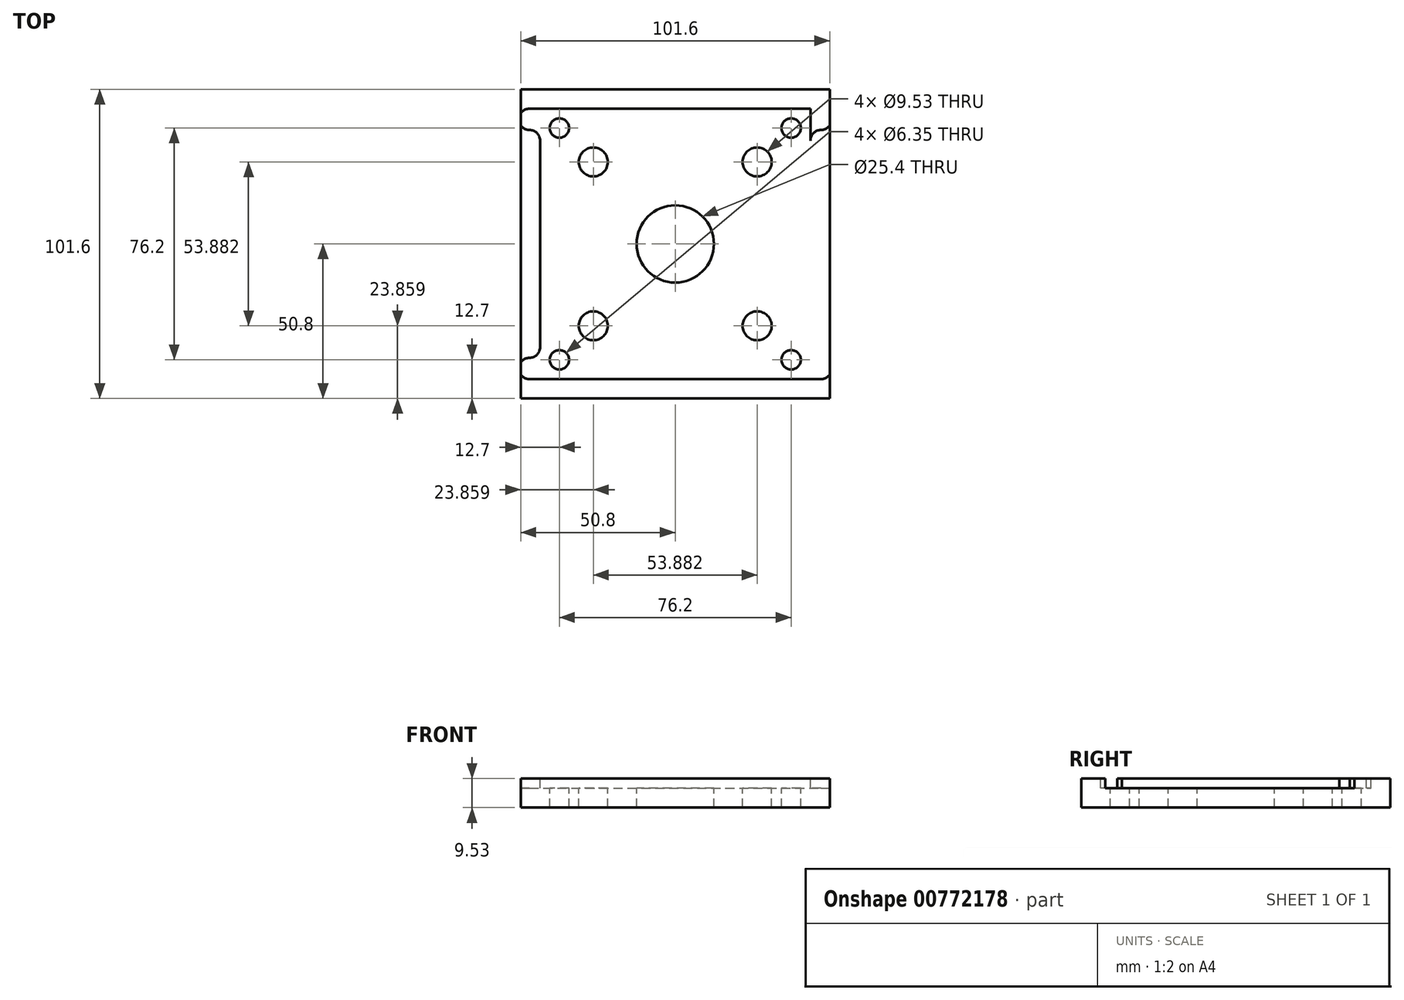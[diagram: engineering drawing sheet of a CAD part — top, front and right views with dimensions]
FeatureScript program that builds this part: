
annotation { "Feature Type Name" : "Feature", "Feature Type Description" : "" }
export const myFeature = defineFeature(function(context is Context, id is Id, definition is map)
    precondition{}
    {
        {
            var Q0;
            Q0=qCreatedBy(makeId("Top.planeOp"),FACE);
            var sketch = newSketch(context, id + "F0", { "sketchPlane" : qUnion([Q0])});
            skLineSegment(sketch, "E0.bottom", {"start": v(0, 0) * mm, "end": v(101.6, 0) * mm});
            skLineSegment(sketch, "E0.top", {"start": v(0, 101.6) * mm, "end": v(101.6, 101.6) * mm});
            skLineSegment(sketch, "E0.left", {"start": v(0, 0) * mm, "end": v(0, 101.6) * mm});
            skLineSegment(sketch, "E0.right", {"start": v(101.6, 0) * mm, "end": v(101.6, 101.6) * mm});
            skSolve(sketch);
        }
        {
            var Q0;
            Q0=makeQuery(id+"F0.imprint","IMPRINT",FACE,{"disambiguationData":[TD([[makeQuery(id+"F0.imprint","IMPRINT",EDGE,{"derivedFrom":sQuery(id+"F0.wireOp",EDGE,"E0.bottom")}),1.0]])]});
            extrude(context, id + "F1", {"entities" : qUnion([Q0]), "depth" : 9.52 * mm, "offsetDistance" : 25.4 * mm});
        }
        {
            var Q0;
            Q0=makeQuery(id+"F1.opExtrude","CAP_FACE",FACE,{"disambiguationData":[OSD([sQuery(id+"F0.wireOp",EDGE,"E0.bottom"),sQuery(id+"F0.wireOp",EDGE,"E0.top"),sQuery(id+"F0.wireOp",EDGE,"E0.left"),sQuery(id+"F0.wireOp",EDGE,"E0.right")])],"isStart":false});
            var sketch = newSketch(context, id + "F2", { "sketchPlane" : qUnion([Q0])});
            skLineSegment(sketch, "E1.bottom", {"start": v(6.35, 6.35) * mm, "end": v(95.25, 6.35) * mm});
            skLineSegment(sketch, "E1.top", {"start": v(6.35, 95.25) * mm, "end": v(95.25, 95.25) * mm});
            skLineSegment(sketch, "E1.left", {"start": v(6.35, 6.35) * mm, "end": v(6.35, 95.25) * mm});
            skLineSegment(sketch, "E1.right", {"start": v(95.25, 6.35) * mm, "end": v(95.25, 95.25) * mm});
            skSolve(sketch);
        }
        {
            var Q0;
            Q0=makeQuery(id+"F2.imprint","IMPRINT",FACE,{"disambiguationData":[TD([[makeQuery(id+"F2.imprint","IMPRINT",EDGE,{"derivedFrom":sQuery(id+"F2.wireOp",EDGE,"E1.bottom")}),1.0]])]});
            extrude(context, id + "F3", {"entities" : qUnion([Q0]), "operationType" : NewBodyOperationType.REMOVE, "oppositeDirection" : true, "depth" : 3.17 * mm, "offsetDistance" : 25.4 * mm});
        }
        {
            var Q0;
            Q0=makeQuery(id+"F1.opExtrude","CAP_FACE",FACE,{"disambiguationData":[OSD([sQuery(id+"F0.wireOp",EDGE,"E0.bottom"),sQuery(id+"F0.wireOp",EDGE,"E0.top"),sQuery(id+"F0.wireOp",EDGE,"E0.left"),sQuery(id+"F0.wireOp",EDGE,"E0.right")])],"isStart":false});
            var sketch = newSketch(context, id + "F4", { "sketchPlane" : qUnion([Q0])});
            skArc(sketch, "E2", {"start": v(2.86, 95.25) * mm, "mid": v(-0.64, 91.76) * mm, "end": v(2.86, 88.27) * mm});
            skLineSegment(sketch, "E3.0.0", {"start": v(95.25, 95.25) * mm, "end": v(6.35, 95.25) * mm});
            skLineSegment(sketch, "E3.0.1", {"start": v(6.35, 95.25) * mm, "end": v(6.35, 6.35) * mm});
            skLineSegment(sketch, "E3.0.2", {"start": v(6.35, 6.35) * mm, "end": v(95.25, 6.35) * mm});
            skLineSegment(sketch, "E3.0.3", {"start": v(95.25, 6.35) * mm, "end": v(95.25, 95.25) * mm});
            skLineSegment(sketch, "E4", {"start": v(6.35, 95.25) * mm, "end": v(2.86, 95.25) * mm});
            skArc(sketch, "E5", {"start": v(6.35, 84.77) * mm, "mid": v(5.33, 87.24) * mm, "end": v(2.86, 88.27) * mm});
            skLineSegment(sketch, "E6", {"start": v(6.35, 84.77) * mm, "end": v(6.35, 95.25) * mm});
            skLineSegment(sketch, "E7", {"start": v(50.8, 95.25) * mm, "end": v(50.8, 6.35) * mm, "construction": true});
            skLineSegment(sketch, "E8", {"start": v(6.35, 50.8) * mm, "end": v(95.25, 50.8) * mm, "construction": true});
            skArc(sketch, "E9.MirrorCS", {"start": v(98.74, 95.25) * mm, "mid": v(102.23, 91.76) * mm, "end": v(98.74, 88.27) * mm});
            skArc(sketch, "E10.MirrorCS", {"start": v(95.25, 84.77) * mm, "mid": v(96.27, 87.24) * mm, "end": v(98.74, 88.27) * mm});
            skLineSegment(sketch, "E11.MirrorCS", {"start": v(95.25, 95.25) * mm, "end": v(98.74, 95.25) * mm});
            skLineSegment(sketch, "E12.MirrorCS", {"start": v(6.35, 6.35) * mm, "end": v(2.86, 6.35) * mm});
            skArc(sketch, "E13.MirrorCS", {"start": v(2.86, 6.35) * mm, "mid": v(-0.64, 9.84) * mm, "end": v(2.86, 13.33) * mm});
            skArc(sketch, "E14.MirrorCS", {"start": v(6.35, 16.83) * mm, "mid": v(5.33, 14.36) * mm, "end": v(2.86, 13.33) * mm});
            skArc(sketch, "E15.MirrorCS", {"start": v(98.74, 6.35) * mm, "mid": v(102.23, 9.84) * mm, "end": v(98.74, 13.33) * mm});
            skLineSegment(sketch, "E16.MirrorCS", {"start": v(95.25, 6.35) * mm, "end": v(98.74, 6.35) * mm});
            skArc(sketch, "E17.MirrorCS", {"start": v(95.25, 16.83) * mm, "mid": v(96.27, 14.36) * mm, "end": v(98.74, 13.33) * mm});
            skSolve(sketch);
        }
        {
            var Q0;
            Q0=makeQuery(id+"F4.imprint","IMPRINT",FACE,{"disambiguationData":[TD([[makeQuery(id+"F4.imprint","IMPRINT",EDGE,{"derivedFrom":sQuery(id+"F4.wireOp",EDGE,"E2")}),1.0]])]});
            var Q1;
            {var subQ0=sQuery(id+"F4.wireOp",EDGE,"E12.MirrorCS");Q1=makeQuery(id+"F4.imprint","IMPRINT",FACE,{"disambiguationData":[TD([[makeQuery(id+"F4.imprint","IMPRINT",EDGE,{"derivedFrom":subQ0}),-1.0]])]});}
            var Q2;
            Q2=makeQuery(id+"F4.imprint","IMPRINT",FACE,{"disambiguationData":[TD([[makeQuery(id+"F4.imprint","IMPRINT",EDGE,{"derivedFrom":sQuery(id+"F4.wireOp",EDGE,"E15.MirrorCS")}),1.0]])]});
            var Q3;
            Q3=makeQuery(id+"F4.imprint","IMPRINT",FACE,{"disambiguationData":[TD([[makeQuery(id+"F4.imprint","IMPRINT",EDGE,{"derivedFrom":sQuery(id+"F4.wireOp",EDGE,"E9.MirrorCS")}),-1.0]])]});
            extrude(context, id + "F5", {"entities" : qUnion([Q0, Q1, Q2, Q3]), "operationType" : NewBodyOperationType.REMOVE, "oppositeDirection" : true, "depth" : 3.17 * mm, "offsetDistance" : 25.4 * mm});
        }
        {
            var Q0;
            {var subQ0=sQuery(id+"F4.wireOp",EDGE,"E3.0.3");Q0=makeQuery(id+"F5.boolean.opBoolean","MERGE",FACE,{"derivedFrom":[makeQuery(id+"F3.boolean.opBoolean","COPY",FACE,{"derivedFrom":makeQuery(id+"F3.opExtrude","CAP_FACE",FACE,{"disambiguationData":[OSD([sQuery(id+"F2.wireOp",EDGE,"E1.bottom"),sQuery(id+"F2.wireOp",EDGE,"E1.top"),sQuery(id+"F2.wireOp",EDGE,"E1.left"),sQuery(id+"F2.wireOp",EDGE,"E1.right")])],"isStart":false})}),makeQuery(id+"F5.opExtrude","CAP_FACE",FACE,{"disambiguationData":[OSD([sQuery(id+"F4.wireOp",EDGE,"E2"),sQuery(id+"F4.wireOp",EDGE,"E4"),sQuery(id+"F4.wireOp",EDGE,"E5"),sQuery(id+"F4.wireOp",EDGE,"E6")])],"isStart":false}),makeQuery(id+"F5.opExtrude","CAP_FACE",FACE,{"disambiguationData":[OSD([sQuery(id+"F4.wireOp",EDGE,"E3.0.1"),sQuery(id+"F4.wireOp",EDGE,"E12.MirrorCS"),sQuery(id+"F4.wireOp",EDGE,"E13.MirrorCS"),sQuery(id+"F4.wireOp",EDGE,"E14.MirrorCS")])],"isStart":false}),makeQuery(id+"F5.opExtrude","CAP_FACE",FACE,{"disambiguationData":[OSD([subQ0,sQuery(id+"F4.wireOp",EDGE,"E15.MirrorCS"),sQuery(id+"F4.wireOp",EDGE,"E16.MirrorCS"),sQuery(id+"F4.wireOp",EDGE,"E17.MirrorCS")])],"isStart":false}),makeQuery(id+"F5.opExtrude","CAP_FACE",FACE,{"disambiguationData":[OSD([subQ0,sQuery(id+"F4.wireOp",EDGE,"E9.MirrorCS"),sQuery(id+"F4.wireOp",EDGE,"E10.MirrorCS"),sQuery(id+"F4.wireOp",EDGE,"E11.MirrorCS")])],"isStart":false})]});}
            var sketch = newSketch(context, id + "F6", { "sketchPlane" : qUnion([Q0])});
            skLineSegment(sketch, "E18.0.0", {"start": v(98.74, 95.25) * mm, "end": v(2.86, 95.25) * mm});
            skArc(sketch, "E18.0.1", {"start": v(2.86, 95.25) * mm, "mid": v(1.25, 94.86) * mm, "end": v(0, 93.77) * mm});
            skArc(sketch, "E18.0.2", {"start": v(5.16, 87.4) * mm, "mid": v(6.04, 86.21) * mm, "end": v(6.35, 84.77) * mm});
            skLineSegment(sketch, "E18.0.3", {"start": v(6.35, 84.77) * mm, "end": v(6.35, 16.83) * mm});
            skArc(sketch, "E18.0.4", {"start": v(6.35, 16.83) * mm, "mid": v(5.33, 14.36) * mm, "end": v(2.86, 13.33) * mm});
            skArc(sketch, "E18.0.5", {"start": v(2.86, 13.33) * mm, "mid": v(-0.64, 9.84) * mm, "end": v(2.86, 6.35) * mm});
            skLineSegment(sketch, "E18.0.6", {"start": v(2.86, 6.35) * mm, "end": v(98.74, 6.35) * mm});
            skArc(sketch, "E18.0.7", {"start": v(98.74, 6.35) * mm, "mid": v(100.35, 6.74) * mm, "end": v(101.6, 7.83) * mm});
            skArc(sketch, "E18.0.8", {"start": v(101.39, 19.1) * mm, "mid": v(99.96, 13.55) * mm, "end": v(95.25, 16.83) * mm});
            skLineSegment(sketch, "E18.0.9", {"start": v(95.25, 16.83) * mm, "end": v(95.25, 84.77) * mm});
            skArc(sketch, "E18.0.10", {"start": v(95.25, 84.77) * mm, "mid": v(96.27, 87.24) * mm, "end": v(98.74, 88.27) * mm});
            skArc(sketch, "E18.0.11", {"start": v(98.74, 88.27) * mm, "mid": v(102.23, 91.76) * mm, "end": v(98.74, 95.25) * mm});
            skLineSegment(sketch, "E19.bottom", {"start": v(6.35, 6.35) * mm, "end": v(95.25, 6.35) * mm, "construction": true});
            skLineSegment(sketch, "E19.top", {"start": v(6.35, 95.25) * mm, "end": v(95.25, 95.25) * mm, "construction": true});
            skLineSegment(sketch, "E19.left", {"start": v(6.35, 6.35) * mm, "end": v(6.35, 95.25) * mm, "construction": true});
            skLineSegment(sketch, "E19.right", {"start": v(95.25, 6.35) * mm, "end": v(95.25, 95.25) * mm, "construction": true});
            skLineSegment(sketch, "E20", {"start": v(6.35, 95.25) * mm, "end": v(95.25, 6.35) * mm, "construction": true});
            skLineSegment(sketch, "E21", {"start": v(6.35, 6.35) * mm, "end": v(95.25, 95.25) * mm, "construction": true});
            skLineSegment(sketch, "E22", {"start": v(6.35, 50.8) * mm, "end": v(95.25, 50.8) * mm, "construction": true});
            skLineSegment(sketch, "E23", {"start": v(50.8, 95.25) * mm, "end": v(50.8, 6.35) * mm, "construction": true});
            skCircle(sketch, "E24", {"center": v(23.86, 77.74) * mm, "radius": 4.76 * mm});
            skCircle(sketch, "E25", {"center": v(77.74, 23.86) * mm, "radius": 4.76 * mm});
            skCircle(sketch, "E26", {"center": v(23.86, 23.86) * mm, "radius": 4.76 * mm});
            skCircle(sketch, "E27", {"center": v(77.74, 77.74) * mm, "radius": 4.76 * mm});
            skPoint(sketch, "E28", {"position": v(50.8, 50.8) * mm});
            skCircle(sketch, "E29", {"center": v(50.8, 50.8) * mm, "radius": 12.7 * mm});
            skSolve(sketch);
        }
        {
            var Q0;
            Q0=makeQuery(id+"F6.imprint","IMPRINT",FACE,{"disambiguationData":[TD([[makeQuery(id+"F6.imprint","IMPRINT",EDGE,{"derivedFrom":sQuery(id+"F6.wireOp",EDGE,"E24")}),1.0]])]});
            var Q1;
            Q1=makeQuery(id+"F6.imprint","IMPRINT",FACE,{"disambiguationData":[TD([[makeQuery(id+"F6.imprint","IMPRINT",EDGE,{"derivedFrom":sQuery(id+"F6.wireOp",EDGE,"E27")}),1.0]])]});
            var Q2;
            Q2=makeQuery(id+"F6.imprint","IMPRINT",FACE,{"disambiguationData":[TD([[makeQuery(id+"F6.imprint","IMPRINT",EDGE,{"derivedFrom":sQuery(id+"F6.wireOp",EDGE,"E25")}),1.0]])]});
            var Q3;
            Q3=makeQuery(id+"F6.imprint","IMPRINT",FACE,{"disambiguationData":[TD([[makeQuery(id+"F6.imprint","IMPRINT",EDGE,{"derivedFrom":sQuery(id+"F6.wireOp",EDGE,"E26")}),1.0]])]});
            var Q4;
            Q4=makeQuery(id+"F6.imprint","IMPRINT",FACE,{"disambiguationData":[TD([[makeQuery(id+"F6.imprint","IMPRINT",EDGE,{"derivedFrom":sQuery(id+"F6.wireOp",EDGE,"E29")}),1.0]])]});
            extrude(context, id + "F7", {"entities" : qUnion([Q0, Q1, Q2, Q3, Q4]), "operationType" : NewBodyOperationType.REMOVE, "endBound" : BoundingType.THROUGH_ALL, "oppositeDirection" : true, "depth" : 25.4 * mm, "offsetDistance" : 25.4 * mm});
        }
        {
            var Q0;
            Q0=makeQuery(id+"F1.opExtrude","CAP_FACE",FACE,{"disambiguationData":[OSD([sQuery(id+"F0.wireOp",EDGE,"E0.bottom"),sQuery(id+"F0.wireOp",EDGE,"E0.top"),sQuery(id+"F0.wireOp",EDGE,"E0.left"),sQuery(id+"F0.wireOp",EDGE,"E0.right")])],"isStart":false});
            var sketch = newSketch(context, id + "F8", { "sketchPlane" : qUnion([Q0])});
            skCircle(sketch, "E30", {"center": v(12.7, 12.7) * mm, "radius": 3.18 * mm});
            skCircle(sketch, "E31", {"center": v(88.9, 88.9) * mm, "radius": 3.18 * mm});
            skCircle(sketch, "E32", {"center": v(12.7, 88.9) * mm, "radius": 3.18 * mm});
            skCircle(sketch, "E33", {"center": v(88.9, 12.7) * mm, "radius": 3.18 * mm});
            skSolve(sketch);
        }
        {
            var Q0;
            Q0=makeQuery(id+"F8.imprint","IMPRINT",FACE,{"disambiguationData":[TD([[makeQuery(id+"F8.imprint","IMPRINT",EDGE,{"derivedFrom":sQuery(id+"F8.wireOp",EDGE,"E30")}),1.0]])]});
            var Q1;
            Q1=makeQuery(id+"F8.imprint","IMPRINT",FACE,{"disambiguationData":[TD([[makeQuery(id+"F8.imprint","IMPRINT",EDGE,{"derivedFrom":sQuery(id+"F8.wireOp",EDGE,"E31")}),1.0]])]});
            var Q2;
            Q2=makeQuery(id+"F8.imprint","IMPRINT",FACE,{"disambiguationData":[TD([[makeQuery(id+"F8.imprint","IMPRINT",EDGE,{"derivedFrom":sQuery(id+"F8.wireOp",EDGE,"E32")}),1.0]])]});
            var Q3;
            Q3=makeQuery(id+"F8.imprint","IMPRINT",FACE,{"disambiguationData":[TD([[makeQuery(id+"F8.imprint","IMPRINT",EDGE,{"derivedFrom":sQuery(id+"F8.wireOp",EDGE,"E33")}),1.0]])]});
            extrude(context, id + "F9", {"entities" : qUnion([Q0, Q1, Q2, Q3]), "operationType" : NewBodyOperationType.REMOVE, "endBound" : BoundingType.THROUGH_ALL, "oppositeDirection" : true, "depth" : 25.4 * mm, "offsetDistance" : 25.4 * mm});
        }
    });
